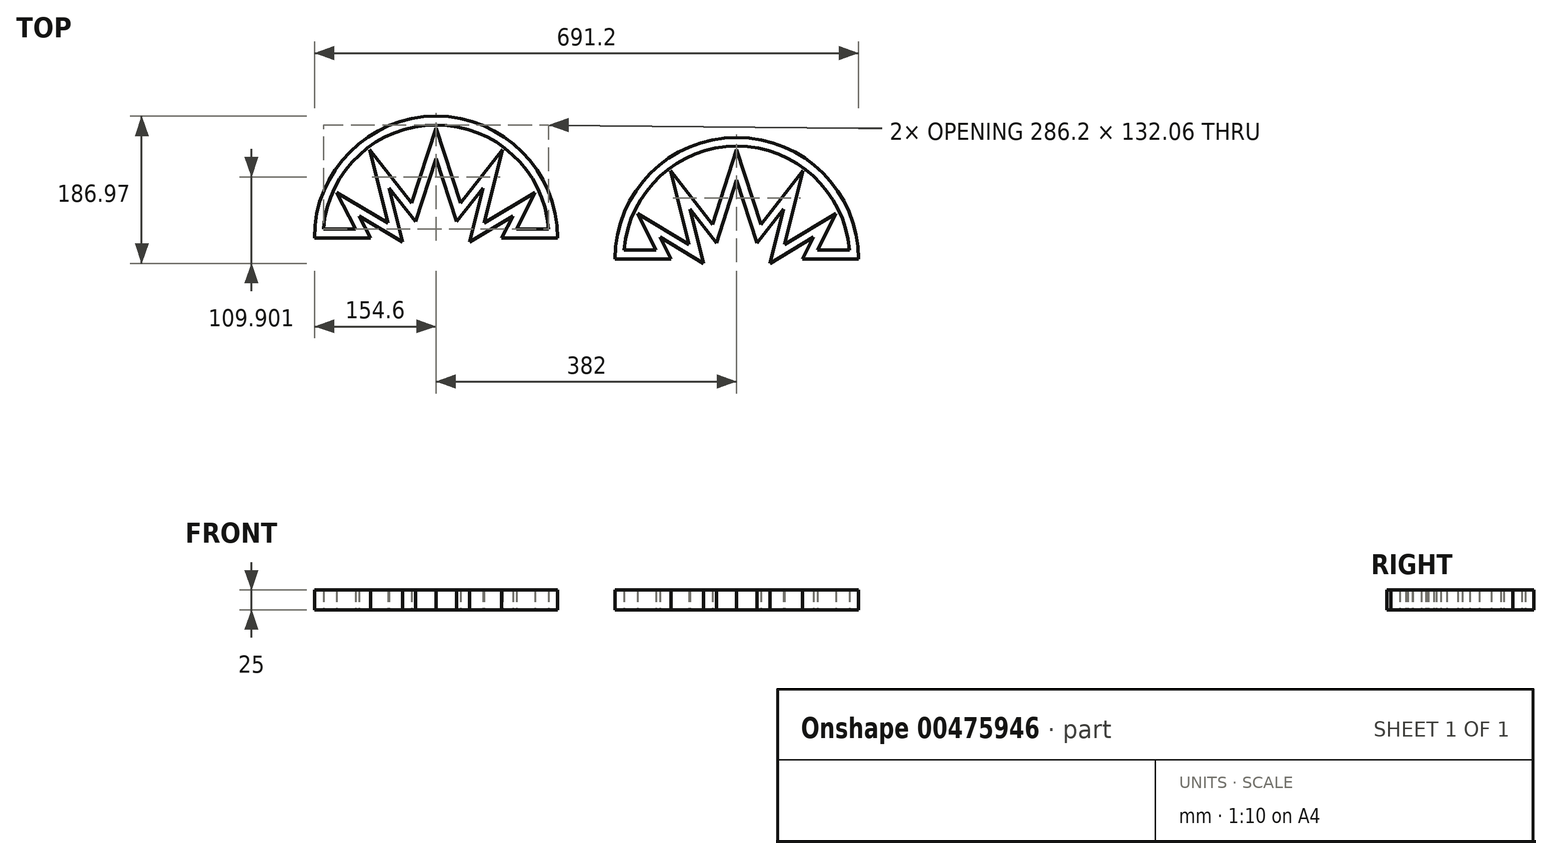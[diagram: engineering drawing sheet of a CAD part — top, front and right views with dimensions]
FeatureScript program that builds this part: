
annotation { "Feature Type Name" : "Feature", "Feature Type Description" : "" }
export const myFeature = defineFeature(function(context is Context, id is Id, definition is map)
    precondition{}
    {
        {
            var Q0;
            Q0=qCreatedBy(makeId("Top.planeOp"),FACE);
            var sketch = newSketch(context, id + "F0", { "sketchPlane" : qUnion([Q0])});
            skLineSegment(sketch, "E0", {"start": v(-154.6, 0) * mm, "end": v(-83.4, 0) * mm});
            skLineSegment(sketch, "E1", {"start": v(-83.4, 0) * mm, "end": v(-97.56, 27.8) * mm});
            skLineSegment(sketch, "E2", {"start": v(-97.56, 27.8) * mm, "end": v(-42.36, -5.37) * mm});
            skLineSegment(sketch, "E3", {"start": v(-42.36, -5.37) * mm, "end": v(-59.54, 63.52) * mm});
            skLineSegment(sketch, "E4", {"start": v(-59.54, 63.52) * mm, "end": v(-25.99, 20.58) * mm});
            skLineSegment(sketch, "E5", {"start": v(-25.99, 20.58) * mm, "end": v(0.8, 103.03) * mm});
            skLineSegment(sketch, "E6", {"start": v(-143.1, 11.5) * mm, "end": v(-102.4, 11.5) * mm});
            skLineSegment(sketch, "E7", {"start": v(-102.4, 11.5) * mm, "end": v(-126, 57.83) * mm});
            skLineSegment(sketch, "E8", {"start": v(-126, 57.83) * mm, "end": v(-60.86, 18.69) * mm});
            skLineSegment(sketch, "E9", {"start": v(-60.86, 18.69) * mm, "end": v(-84.26, 112.52) * mm});
            skLineSegment(sketch, "E10", {"start": v(-84.26, 112.52) * mm, "end": v(-30.94, 44.28) * mm});
            skLineSegment(sketch, "E11", {"start": v(-30.94, 44.28) * mm, "end": v(0.58, 141.28) * mm});
            skArc(sketch, "E12", {"start": v(-143.1, 11.5) * mm, "mid": v(-97.1, 105.73) * mm, "end": v(0.7, 143.56) * mm});
            skArc(sketch, "E13", {"start": v(-154.6, 0) * mm, "mid": v(-109.06, 109.58) * mm, "end": v(0.74, 154.6) * mm});
            skLineSegment(sketch, "E14.MirrorCS", {"start": v(154.6, 0) * mm, "end": v(83.4, 0) * mm});
            skArc(sketch, "E15.MirrorCS", {"start": v(143.1, 11.5) * mm, "mid": v(97.1, 105.73) * mm, "end": v(-0.7, 143.56) * mm});
            skLineSegment(sketch, "E16.MirrorCS", {"start": v(102.4, 11.5) * mm, "end": v(126, 57.83) * mm});
            skLineSegment(sketch, "E17.MirrorCS", {"start": v(42.36, -5.37) * mm, "end": v(59.54, 63.52) * mm});
            skLineSegment(sketch, "E18.MirrorCS", {"start": v(59.54, 63.52) * mm, "end": v(25.99, 20.58) * mm});
            skLineSegment(sketch, "E19.MirrorCS", {"start": v(97.56, 27.8) * mm, "end": v(42.36, -5.37) * mm});
            skLineSegment(sketch, "E20.MirrorCS", {"start": v(83.4, 0) * mm, "end": v(97.56, 27.8) * mm});
            skLineSegment(sketch, "E21.MirrorCS", {"start": v(30.94, 44.28) * mm, "end": v(-0.58, 141.28) * mm});
            skArc(sketch, "E22.MirrorCS", {"start": v(154.6, 0) * mm, "mid": v(109.06, 109.58) * mm, "end": v(-0.74, 154.6) * mm});
            skLineSegment(sketch, "E23.MirrorCS", {"start": v(84.26, 112.52) * mm, "end": v(30.94, 44.28) * mm});
            skLineSegment(sketch, "E24.MirrorCS", {"start": v(60.86, 18.69) * mm, "end": v(84.26, 112.52) * mm});
            skLineSegment(sketch, "E25.MirrorCS", {"start": v(25.99, 20.58) * mm, "end": v(-0.8, 103.03) * mm});
            skLineSegment(sketch, "E26.MirrorCS", {"start": v(143.1, 11.5) * mm, "end": v(102.4, 11.5) * mm});
            skLineSegment(sketch, "E27.MirrorCS", {"start": v(126, 57.83) * mm, "end": v(60.86, 18.69) * mm});
            skSolve(sketch);
        }
        {
            var Q0;
            Q0 = qSketchRegion(id + "F0", true);
            extrude(context, id + "F1", {"entities" : qUnion([Q0]), "depth" : 25 * mm});
        }
        {
            var Q0;
            Q0=makeQuery(id+"F1.opExtrude","SWEPT_BODY",BODY,{"disambiguationData":[OSD([sQuery(id+"F0.wireOp",EDGE,"E0"),sQuery(id+"F0.wireOp",EDGE,"E1"),sQuery(id+"F0.wireOp",EDGE,"E2"),sQuery(id+"F0.wireOp",EDGE,"E3"),sQuery(id+"F0.wireOp",EDGE,"E4"),sQuery(id+"F0.wireOp",EDGE,"E5"),sQuery(id+"F0.wireOp",EDGE,"E6"),sQuery(id+"F0.wireOp",EDGE,"E7"),sQuery(id+"F0.wireOp",EDGE,"E8"),sQuery(id+"F0.wireOp",EDGE,"E9"),sQuery(id+"F0.wireOp",EDGE,"E10"),sQuery(id+"F0.wireOp",EDGE,"E11"),sQuery(id+"F0.wireOp",EDGE,"E12"),sQuery(id+"F0.wireOp",EDGE,"E13"),sQuery(id+"F0.wireOp",EDGE,"E15.MirrorCS"),sQuery(id+"F0.wireOp",EDGE,"E16.MirrorCS"),sQuery(id+"F0.wireOp",EDGE,"E17.MirrorCS"),sQuery(id+"F0.wireOp",EDGE,"E18.MirrorCS"),sQuery(id+"F0.wireOp",EDGE,"E19.MirrorCS"),sQuery(id+"F0.wireOp",EDGE,"E20.MirrorCS"),sQuery(id+"F0.wireOp",EDGE,"E21.MirrorCS"),sQuery(id+"F0.wireOp",EDGE,"E22.MirrorCS"),sQuery(id+"F0.wireOp",EDGE,"E14.MirrorCS"),sQuery(id+"F0.wireOp",EDGE,"E23.MirrorCS"),sQuery(id+"F0.wireOp",EDGE,"E24.MirrorCS"),sQuery(id+"F0.wireOp",EDGE,"E25.MirrorCS"),sQuery(id+"F0.wireOp",EDGE,"E26.MirrorCS"),sQuery(id+"F0.wireOp",EDGE,"E27.MirrorCS")])]});
            transform(context, id + "F2", {"entities" : qUnion([Q0]), "transformType" : TransformType.TRANSLATION_3D, "dx" : 382 * mm, "dy" : -27 * mm, "dz" : 0 * mm, "makeCopy" : true});
        }
    });
